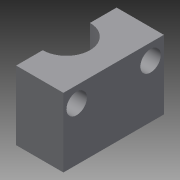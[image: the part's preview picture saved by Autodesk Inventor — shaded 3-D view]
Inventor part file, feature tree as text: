
AUTODESK INVENTOR PART (.ipt)
format: ipt  version: 2015 (Build 190159000, 159)  size: 107,520 bytes
history: native  units: in
note: dims shown in document units (in); Inventor stores cm internally (conversion verified against a paired STEP export)
features: extrude x3, sketch x2
ambient origin geometry x8: Origin, YZ Plane, XZ Plane, XY Plane, X Axis, Y Axis, Z Axis, Center Point
bodies: Body1 (feature_tree)
feature tree (5):
  sketch  "Sketch1"  dims[d0=0.7677in d1=0.4724in]
  extrude  "Extrusion4"  Depth=0.4724in
  extrude  "Extrusion5"  Depth=0.1181in
  extrude  "Extrusion6"  Depth=0.4724in
  sketch  "Sketch3"  dims[d2=0.1181in d3=0.1181in d4=0.4724in d15=0.4331in d16=0.2559in d17=0.0in d18=0.0in d19=0.1181in d20=0.1378in d21=0.0in d22=0.0in d23=0.2047in d24=0.2047in d25=1.1811in d26=0.0in]
